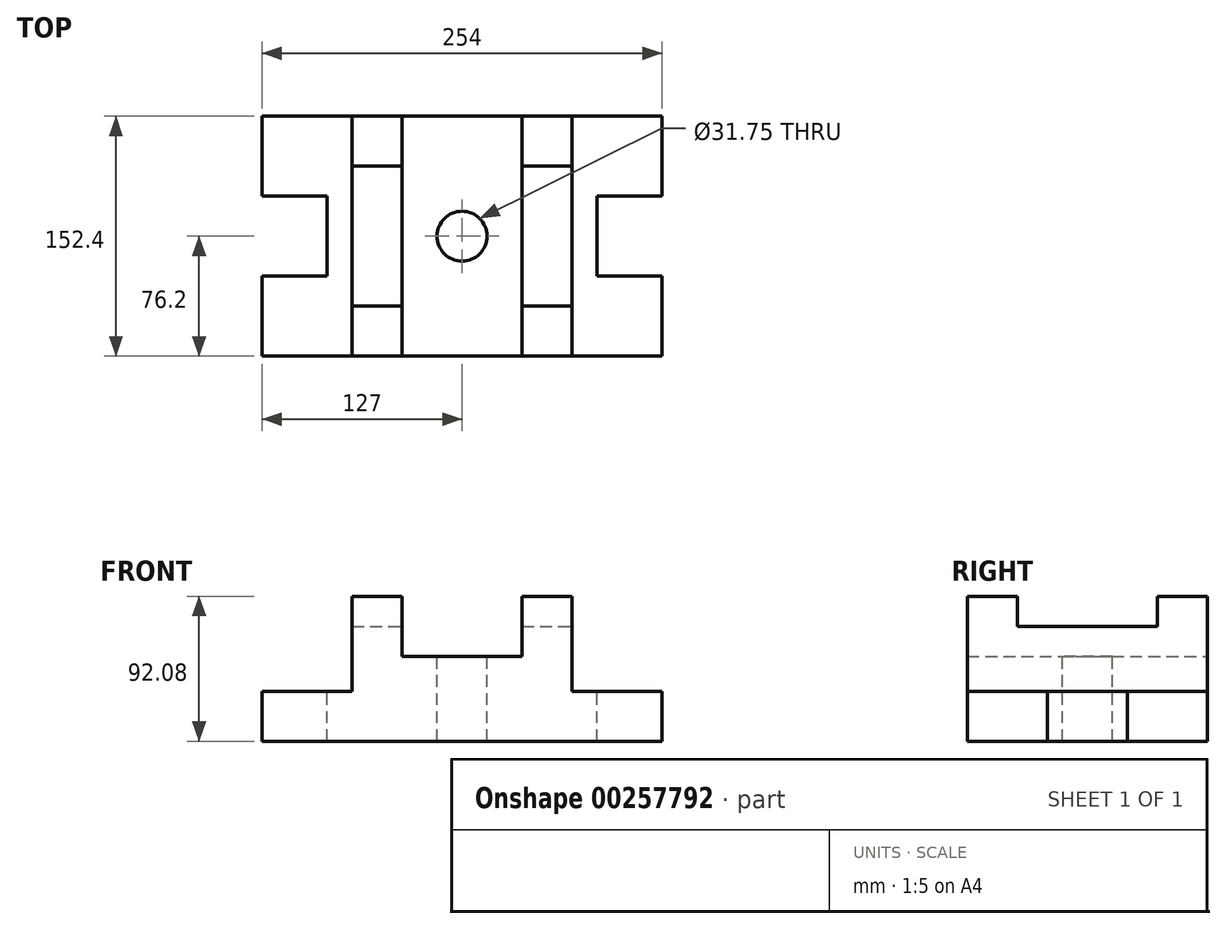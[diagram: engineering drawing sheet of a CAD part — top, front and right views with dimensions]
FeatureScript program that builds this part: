
annotation { "Feature Type Name" : "Feature", "Feature Type Description" : "" }
export const myFeature = defineFeature(function(context is Context, id is Id, definition is map)
    precondition{}
    {
        {
            var Q0;
            Q0=qCreatedBy(makeId("Front.planeOp"),FACE);
            var sketch = newSketch(context, id + "F0", { "sketchPlane" : qUnion([Q0])});
            skLineSegment(sketch, "E0", {"start": v(0, 0) * mm, "end": v(254, 0) * mm});
            skLineSegment(sketch, "E1", {"start": v(0, 0) * mm, "end": v(0, 31.75) * mm});
            skLineSegment(sketch, "E2", {"start": v(0, 31.75) * mm, "end": v(57.15, 31.75) * mm});
            skLineSegment(sketch, "E3", {"start": v(57.15, 31.75) * mm, "end": v(57.15, 92.08) * mm});
            skLineSegment(sketch, "E4", {"start": v(57.15, 92.08) * mm, "end": v(88.9, 92.08) * mm});
            skLineSegment(sketch, "E5", {"start": v(165.1, 92.08) * mm, "end": v(196.85, 92.08) * mm});
            skLineSegment(sketch, "E6", {"start": v(88.9, 92.08) * mm, "end": v(88.9, 53.98) * mm});
            skLineSegment(sketch, "E7", {"start": v(88.9, 53.98) * mm, "end": v(165.1, 53.98) * mm});
            skLineSegment(sketch, "E8", {"start": v(165.1, 53.98) * mm, "end": v(165.1, 92.08) * mm});
            skLineSegment(sketch, "E9", {"start": v(196.85, 92.08) * mm, "end": v(196.85, 31.75) * mm});
            skLineSegment(sketch, "E10", {"start": v(196.85, 31.75) * mm, "end": v(254, 31.75) * mm});
            skLineSegment(sketch, "E11", {"start": v(254, 0) * mm, "end": v(254, 31.75) * mm});
            skSolve(sketch);
        }
        {
            var Q0;
            Q0=makeQuery(id+"F0.imprint","IMPRINT",FACE,{"disambiguationData":[TD([[makeQuery(id+"F0.imprint","IMPRINT",EDGE,{"derivedFrom":sQuery(id+"F0.wireOp",EDGE,"E0")}),1.0]])]});
            extrude(context, id + "F1", {"entities" : qUnion([Q0]), "depth" : 152.4 * mm});
        }
        {
            var Q0;
            Q0=makeQuery(id+"F1.opExtrude","SWEPT_FACE",FACE,{"disambiguationData":[OSD([sQuery(id+"F0.wireOp",EDGE,"E10")])]});
            var sketch = newSketch(context, id + "F2", { "sketchPlane" : qUnion([Q0])});
            skLineSegment(sketch, "E12.bottom", {"start": v(254, -101.6) * mm, "end": v(212.72, -101.6) * mm});
            skLineSegment(sketch, "E12.top", {"start": v(254, -50.8) * mm, "end": v(212.72, -50.8) * mm});
            skLineSegment(sketch, "E12.left", {"start": v(254, -101.6) * mm, "end": v(254, -50.8) * mm});
            skLineSegment(sketch, "E12.right", {"start": v(212.72, -101.6) * mm, "end": v(212.72, -50.8) * mm});
            skSolve(sketch);
        }
        {
            var Q0;
            Q0=makeQuery(id+"F2.imprint","IMPRINT",FACE,{"disambiguationData":[TD([[makeQuery(id+"F2.imprint","IMPRINT",EDGE,{"derivedFrom":sQuery(id+"F2.wireOp",EDGE,"E12.bottom")}),-1.0]])]});
            extrude(context, id + "F3", {"entities" : qUnion([Q0]), "operationType" : NewBodyOperationType.REMOVE, "oppositeDirection" : true, "depth" : 31.75 * mm});
        }
        {
            var Q0;
            Q0=makeQuery(id+"F1.opExtrude","SWEPT_FACE",FACE,{"disambiguationData":[OSD([sQuery(id+"F0.wireOp",EDGE,"E2")])]});
            var sketch = newSketch(context, id + "F4", { "sketchPlane" : qUnion([Q0])});
            skLineSegment(sketch, "E13.bottom", {"start": v(0, -101.6) * mm, "end": v(41.28, -101.6) * mm});
            skLineSegment(sketch, "E13.top", {"start": v(0, -50.8) * mm, "end": v(41.28, -50.8) * mm});
            skLineSegment(sketch, "E13.left", {"start": v(0, -101.6) * mm, "end": v(0, -50.8) * mm});
            skLineSegment(sketch, "E13.right", {"start": v(41.28, -101.6) * mm, "end": v(41.27, -50.8) * mm});
            skSolve(sketch);
        }
        {
            var Q0;
            Q0=makeQuery(id+"F4.imprint","IMPRINT",FACE,{"disambiguationData":[TD([[makeQuery(id+"F4.imprint","IMPRINT",EDGE,{"derivedFrom":sQuery(id+"F4.wireOp",EDGE,"E13.bottom")}),1.0]])]});
            extrude(context, id + "F5", {"entities" : qUnion([Q0]), "operationType" : NewBodyOperationType.REMOVE, "oppositeDirection" : true, "depth" : 31.75 * mm});
        }
        {
            var Q0;
            Q0=makeQuery(id+"F1.opExtrude","SWEPT_FACE",FACE,{"disambiguationData":[OSD([sQuery(id+"F0.wireOp",EDGE,"E9")])]});
            var sketch = newSketch(context, id + "F6", { "sketchPlane" : qUnion([Q0])});
            skLineSegment(sketch, "E14.bottom", {"start": v(-120.65, 92.08) * mm, "end": v(-31.75, 92.08) * mm});
            skLineSegment(sketch, "E14.top", {"start": v(-120.65, 73.03) * mm, "end": v(-31.75, 73.03) * mm});
            skLineSegment(sketch, "E14.left", {"start": v(-120.65, 92.08) * mm, "end": v(-120.65, 73.03) * mm});
            skLineSegment(sketch, "E14.right", {"start": v(-31.75, 92.08) * mm, "end": v(-31.75, 73.03) * mm});
            skSolve(sketch);
        }
        {
            var Q0;
            Q0=makeQuery(id+"F6.imprint","IMPRINT",FACE,{"disambiguationData":[TD([[makeQuery(id+"F6.imprint","IMPRINT",EDGE,{"derivedFrom":sQuery(id+"F6.wireOp",EDGE,"E14.bottom")}),-1.0]])]});
            extrude(context, id + "F7", {"entities" : qUnion([Q0]), "operationType" : NewBodyOperationType.REMOVE, "oppositeDirection" : true, "depth" : 254 * mm});
        }
        {
            var Q0;
            Q0=makeQuery(id+"F1.opExtrude","SWEPT_FACE",FACE,{"disambiguationData":[OSD([sQuery(id+"F0.wireOp",EDGE,"E7")])]});
            var sketch = newSketch(context, id + "F8", { "sketchPlane" : qUnion([Q0])});
            skPoint(sketch, "E15", {"position": v(127, 0) * mm});
            skLineSegment(sketch, "E16", {"start": v(127, 0) * mm, "end": v(127, -76.2) * mm, "construction": true});
            skCircle(sketch, "E17", {"center": v(127, -76.2) * mm, "radius": 15.88 * mm});
            skSolve(sketch);
        }
        {
            var Q0;
            Q0=makeQuery(id+"F8.imprint","IMPRINT",FACE,{"disambiguationData":[TD([[makeQuery(id+"F8.imprint","IMPRINT",EDGE,{"derivedFrom":sQuery(id+"F8.wireOp",EDGE,"E17")}),1.0]])]});
            extrude(context, id + "F9", {"entities" : qUnion([Q0]), "operationType" : NewBodyOperationType.REMOVE, "oppositeDirection" : true, "depth" : 101.6 * mm});
        }
    });
